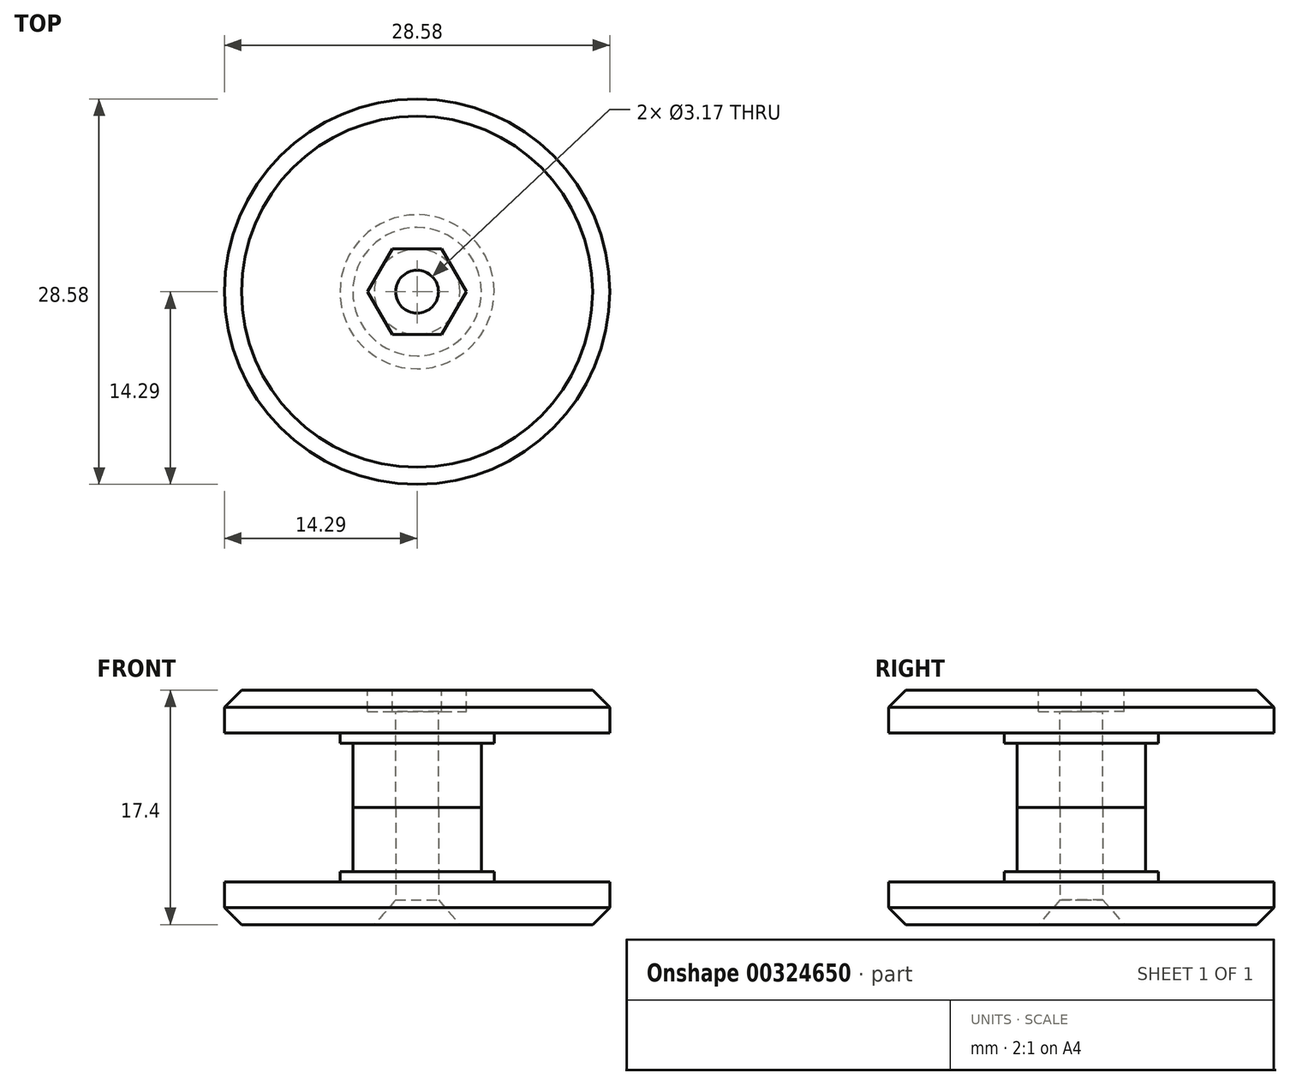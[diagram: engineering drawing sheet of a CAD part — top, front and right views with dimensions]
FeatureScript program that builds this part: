
annotation { "Feature Type Name" : "Feature", "Feature Type Description" : "" }
export const myFeature = defineFeature(function(context is Context, id is Id, definition is map)
    precondition{}
    {
        {
            var Q0;
            Q0=qCreatedBy(makeId("Right.planeOp"),FACE);
            var sketch = newSketch(context, id + "F0", { "sketchPlane" : qUnion([Q0])});
            skLineSegment(sketch, "E0", {"start": v(0, 8.7) * mm, "end": v(0, 0) * mm, "construction": true});
            skLineSegment(sketch, "E1", {"start": v(-13.02, 8.7) * mm, "end": v(-3.18, 8.7) * mm});
            skLineSegment(sketch, "E2", {"start": v(-3.18, 8.7) * mm, "end": v(-3.18, 7.11) * mm});
            skLineSegment(sketch, "E3", {"start": v(-3.18, 7.11) * mm, "end": v(-1.59, 7.11) * mm});
            skLineSegment(sketch, "E4", {"start": v(-1.59, 7.11) * mm, "end": v(-1.59, 0) * mm});
            skLineSegment(sketch, "E5", {"start": v(-1.59, 0) * mm, "end": v(-4.76, 0) * mm});
            skLineSegment(sketch, "E6", {"start": v(-4.76, 0) * mm, "end": v(-4.76, 4.76) * mm});
            skLineSegment(sketch, "E7", {"start": v(-4.76, 4.76) * mm, "end": v(-5.72, 4.76) * mm});
            skLineSegment(sketch, "E8", {"start": v(-5.72, 4.76) * mm, "end": v(-5.72, 5.52) * mm});
            skLineSegment(sketch, "E9", {"start": v(-5.72, 5.52) * mm, "end": v(-14.29, 5.52) * mm});
            skLineSegment(sketch, "E10", {"start": v(-14.29, 5.52) * mm, "end": v(-14.29, 7.43) * mm});
            skLineSegment(sketch, "E11", {"start": v(-14.29, 7.43) * mm, "end": v(-13.02, 8.7) * mm});
            skSolve(sketch);
        }
        {
            var Q0;
            Q0=makeQuery(id+"F0.imprint","IMPRINT",FACE,{"disambiguationData":[TD([[makeQuery(id+"F0.imprint","IMPRINT",EDGE,{"derivedFrom":sQuery(id+"F0.wireOp",EDGE,"E1")}),-1.0]])]});
            var Q1;
            Q1=sQuery(id+"F0.wireOp",EDGE,"E0");
            revolve(context, id + "F1", {"entities" : qUnion([Q0]), "axis" : qUnion([Q1]), "revolveType" : RevolveType.FULL});
        }
        {
            var Q0;
            Q0=makeQuery(id+"F1.opRevolve","SWEPT_FACE",FACE,{"disambiguationData":[OSD([sQuery(id+"F0.wireOp",EDGE,"E1")])]});
            var sketch = newSketch(context, id + "F2", { "sketchPlane" : qUnion([Q0])});
            skCircle(sketch, "E12.cCircle", {"center": v(0, 0) * mm, "radius": 3.67 * mm, "construction": true});
            skLineSegment(sketch, "E12.0", {"start": v(-1.83, -3.18) * mm, "end": v(-3.67, 0) * mm});
            skLineSegment(sketch, "E12.1", {"start": v(-3.67, 0) * mm, "end": v(-1.83, 3.18) * mm});
            skLineSegment(sketch, "E12.2", {"start": v(-1.83, 3.18) * mm, "end": v(1.83, 3.18) * mm});
            skLineSegment(sketch, "E12.3", {"start": v(1.83, 3.18) * mm, "end": v(3.67, 0) * mm});
            skLineSegment(sketch, "E12.4", {"start": v(3.67, 0) * mm, "end": v(1.83, -3.18) * mm});
            skLineSegment(sketch, "E12.5", {"start": v(1.83, -3.18) * mm, "end": v(-1.83, -3.18) * mm});
            skSolve(sketch);
        }
        {
            var Q0;
            {var subQ0=sQuery(id+"F2.wireOp",EDGE,"E12.3");var subQ1=sQuery(id+"F2.wireOp",EDGE,"E12.2");var subQ2=makeQuery(id+"F2.imprint","INTERSECT",VERTEX,{"derivedFrom":[subQ1,subQ0]});Q0=makeQuery(id+"F2.imprint","IMPRINT",FACE,{"disambiguationData":[TD([[makeQuery(id+"F2.imprint","IMPRINT",EDGE,{"disambiguationData":[TD([[subQ2,1.0]])],"derivedFrom":subQ1}),-1.0]])]});}
            var Q1;
            {var subQ0=sQuery(id+"F2.wireOp",EDGE,"E12.4");var subQ1=sQuery(id+"F2.wireOp",EDGE,"E12.3");var subQ2=makeQuery(id+"F2.imprint","INTERSECT",VERTEX,{"derivedFrom":[subQ1,subQ0]});Q1=makeQuery(id+"F2.imprint","IMPRINT",FACE,{"disambiguationData":[TD([[makeQuery(id+"F2.imprint","IMPRINT",EDGE,{"disambiguationData":[TD([[subQ2,1.0]])],"derivedFrom":subQ1}),-1.0]])]});}
            var Q2;
            {var subQ0=sQuery(id+"F2.wireOp",EDGE,"E12.5");var subQ1=sQuery(id+"F2.wireOp",EDGE,"E12.4");var subQ2=makeQuery(id+"F2.imprint","INTERSECT",VERTEX,{"derivedFrom":[subQ1,subQ0]});Q2=makeQuery(id+"F2.imprint","IMPRINT",FACE,{"disambiguationData":[TD([[makeQuery(id+"F2.imprint","IMPRINT",EDGE,{"disambiguationData":[TD([[subQ2,1.0]])],"derivedFrom":subQ1}),-1.0]])]});}
            var Q3;
            {var subQ0=sQuery(id+"F2.wireOp",EDGE,"E12.5");var subQ1=sQuery(id+"F2.wireOp",EDGE,"E12.0");var subQ2=makeQuery(id+"F2.imprint","INTERSECT",VERTEX,{"derivedFrom":[subQ1,subQ0]});Q3=makeQuery(id+"F2.imprint","IMPRINT",FACE,{"disambiguationData":[TD([[makeQuery(id+"F2.imprint","IMPRINT",EDGE,{"disambiguationData":[TD([[subQ2,-1.0]])],"derivedFrom":subQ1}),-1.0]])]});}
            var Q4;
            {var subQ0=sQuery(id+"F2.wireOp",EDGE,"E12.1");var subQ1=sQuery(id+"F2.wireOp",EDGE,"E12.0");var subQ2=makeQuery(id+"F2.imprint","INTERSECT",VERTEX,{"derivedFrom":[subQ1,subQ0]});Q4=makeQuery(id+"F2.imprint","IMPRINT",FACE,{"disambiguationData":[TD([[makeQuery(id+"F2.imprint","IMPRINT",EDGE,{"disambiguationData":[TD([[subQ2,1.0]])],"derivedFrom":subQ1}),-1.0]])]});}
            var Q5;
            {var subQ0=sQuery(id+"F2.wireOp",EDGE,"E12.2");var subQ1=sQuery(id+"F2.wireOp",EDGE,"E12.1");var subQ2=makeQuery(id+"F2.imprint","INTERSECT",VERTEX,{"derivedFrom":[subQ1,subQ0]});Q5=makeQuery(id+"F2.imprint","IMPRINT",FACE,{"disambiguationData":[TD([[makeQuery(id+"F2.imprint","IMPRINT",EDGE,{"disambiguationData":[TD([[subQ2,1.0]])],"derivedFrom":subQ1}),-1.0]])]});}
            var Q6;
            Q6=makeQuery(id+"F1.opRevolve","SWEPT_FACE",FACE,{"disambiguationData":[OSD([sQuery(id+"F0.wireOp",EDGE,"E3")])]});
            extrude(context, id + "F3", {"entities" : qUnion([Q0, Q1, Q2, Q3, Q4, Q5]), "operationType" : NewBodyOperationType.REMOVE, "endBound" : BoundingType.UP_TO_SURFACE, "oppositeDirection" : true, "endBoundEntityFace" : qUnion([Q6]), "depth" : 25.4 * mm});
        }
        {
            var Q0;
            Q0=qCreatedBy(makeId("Right.planeOp"),FACE);
            var sketch = newSketch(context, id + "F4", { "sketchPlane" : qUnion([Q0])});
            skLineSegment(sketch, "E13", {"start": v(-4.76, 0) * mm, "end": v(-4.76, -4.76) * mm});
            skLineSegment(sketch, "E14", {"start": v(-4.76, -4.76) * mm, "end": v(-5.72, -4.76) * mm});
            skLineSegment(sketch, "E15", {"start": v(-5.72, -4.76) * mm, "end": v(-5.72, -5.52) * mm});
            skLineSegment(sketch, "E16", {"start": v(-5.72, -5.52) * mm, "end": v(-14.29, -5.52) * mm});
            skLineSegment(sketch, "E17", {"start": v(-14.29, -5.52) * mm, "end": v(-14.29, -7.43) * mm});
            skLineSegment(sketch, "E18", {"start": v(-14.29, -7.43) * mm, "end": v(-13.02, -8.7) * mm});
            skLineSegment(sketch, "E19", {"start": v(-13.02, -8.7) * mm, "end": v(0, -8.7) * mm});
            skLineSegment(sketch, "E20", {"start": v(0, -8.7) * mm, "end": v(0, 0) * mm});
            skLineSegment(sketch, "E21", {"start": v(-4.76, 0) * mm, "end": v(0, 0) * mm});
            skSolve(sketch);
        }
        {
            var Q0;
            Q0=makeQuery(id+"F4.imprint","IMPRINT",FACE,{"disambiguationData":[TD([[makeQuery(id+"F4.imprint","IMPRINT",EDGE,{"derivedFrom":sQuery(id+"F4.wireOp",EDGE,"E13")}),1.0]])]});
            var Q1;
            Q1=makeQuery(id+"F1.opRevolve","SWEPT_FACE",FACE,{"disambiguationData":[OSD([sQuery(id+"F0.wireOp",EDGE,"E6")])]});
            revolve(context, id + "F5", {"entities" : qUnion([Q0]), "axis" : qUnion([Q1]), "revolveType" : RevolveType.FULL});
        }
        {
            var Q0;
            Q0=makeQuery(id+"F5.opRevolve","SWEPT_FACE",FACE,{"disambiguationData":[OSD([sQuery(id+"F4.wireOp",EDGE,"E19")])]});
            var sketch = newSketch(context, id + "F6", { "sketchPlane" : qUnion([Q0])});
            skPoint(sketch, "E22", {"position": v(0, 0) * mm});
            skSolve(sketch);
        }
        {
            var Q0;
            Q0=sQuery(id+"F6.wireOp",VERTEX,"E22");
            var Q1;
            Q1=makeQuery(id+"F5.opRevolve","SWEPT_BODY",BODY,{"disambiguationData":[OSD([sQuery(id+"F4.wireOp",EDGE,"E13"),sQuery(id+"F4.wireOp",EDGE,"E14"),sQuery(id+"F4.wireOp",EDGE,"E15"),sQuery(id+"F4.wireOp",EDGE,"E16"),sQuery(id+"F4.wireOp",EDGE,"E17"),sQuery(id+"F4.wireOp",EDGE,"E18"),sQuery(id+"F4.wireOp",EDGE,"E19"),sQuery(id+"F4.wireOp",EDGE,"E20"),sQuery(id+"F4.wireOp",EDGE,"E21")])]});
            hole(context, id + "F7", {"style" : HoleStyle.C_SINK, "endStyle" : HoleEndStyle.BLIND, "holeDiameter" : 3.17 * mm, "cSinkDiameter" : 6.35 * mm, "cSinkAngle" : 82 * degree, "holeDepth" : 15.88 * mm, "tappedDepth" : 12.7 * mm, "tapClearance" : 3, "locations" : qUnion([Q0]), "scope" : qUnion([Q1])});
        }
    });
